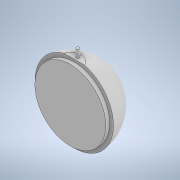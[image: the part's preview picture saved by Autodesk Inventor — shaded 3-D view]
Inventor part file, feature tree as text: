
AUTODESK INVENTOR PART (.ipt)
format: ipt  version: 2022 (Build 260153000, 153)  size: 141,312 bytes
history: native  units: in
note: dims shown in document units (in); Inventor stores cm internally (conversion verified against a paired STEP export)
features: sketch x5, extrude x4, revolve x1
ambient origin geometry x8: Origin, YZ Plane, XZ Plane, XY Plane, X Axis, Y Axis, Z Axis, Center Point
bodies: Body1 (feature_tree)
feature tree (10):
  revolve  "Revolution2"  [1 undecoded]
  extrude  "Extrusion5"  Depth=1.25in TaperAngle=0.0deg
  extrude  "Extrusion6"  Depth=0.1125in
  extrude  "Extrusion7"  Depth=0.25in TaperAngle=0.0deg
  extrude  "Extrusion8"  Depth=0.0344in
  sketch  "Sketch6"  dims[d19=180.0deg d20=0.125in d21=0.0in]
  sketch  "Sketch9"  dims[d23=0.125in d24=0.0in d25=1.2in d26=1.25in d27=0.0in d28=0.0in]
  sketch  "Sketch10"  dims[d29=0.225in d30=0.1125in]
  sketch  "Sketch11"  dims[d31=0.1in d32=0.25in d33=0.0in]
  sketch  "Sketch12"  dims[d10=0.5in d11=0.0344in d12=0.5in d13=0.0344in]
note: 1 required parameter value undecoded (feature->parameter linkage not recoverable at this tier; creation-order binding heuristic only, values carry confidence <= 0.55)
